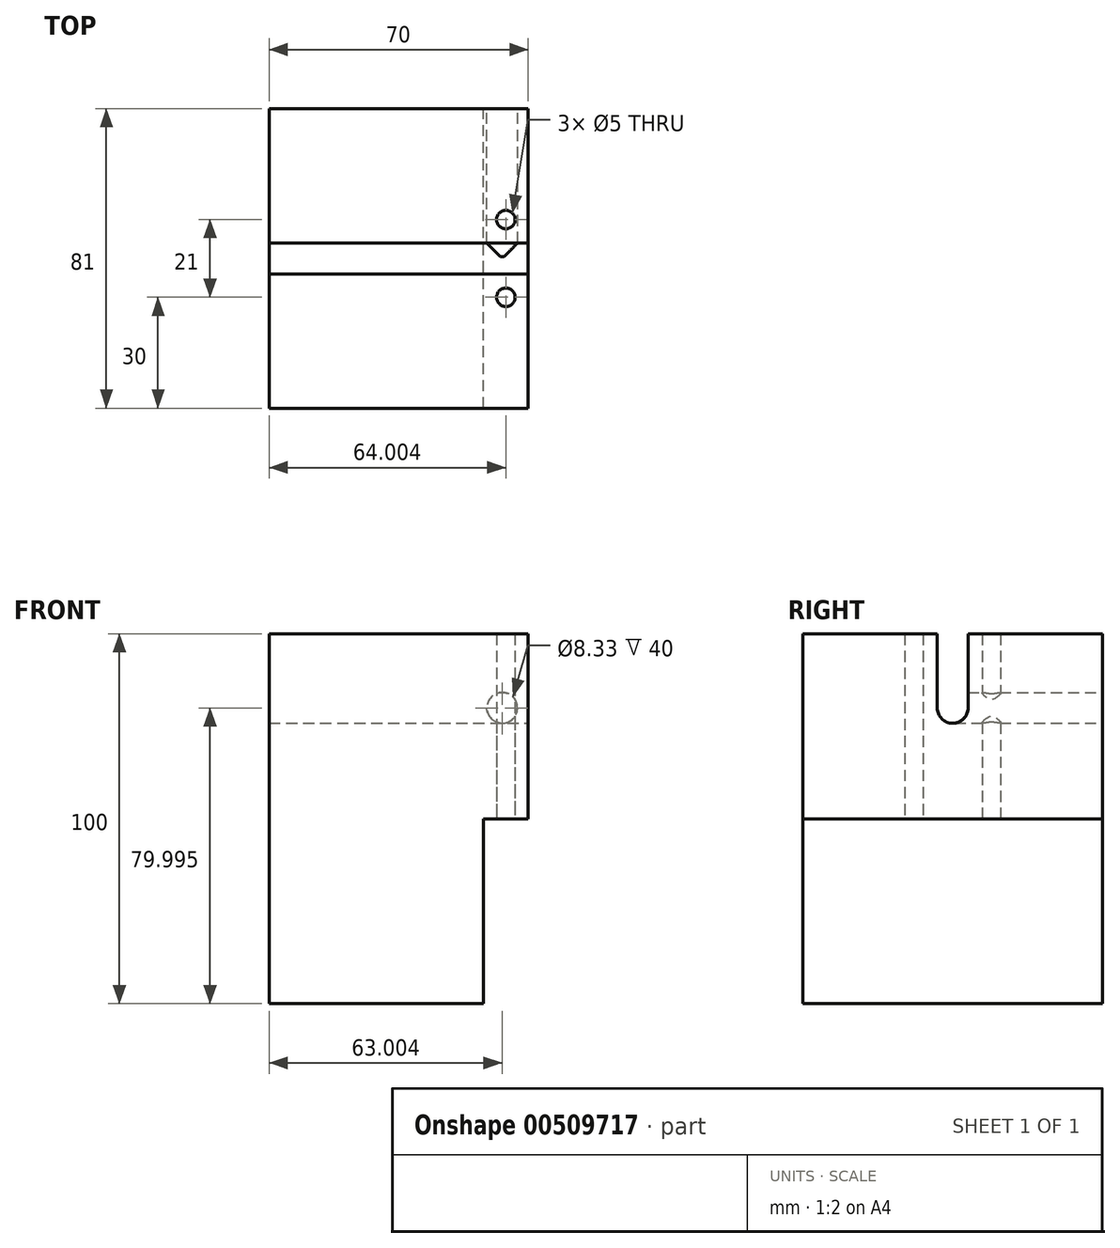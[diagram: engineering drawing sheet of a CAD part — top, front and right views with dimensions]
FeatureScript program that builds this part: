
annotation { "Feature Type Name" : "Feature", "Feature Type Description" : "" }
export const myFeature = defineFeature(function(context is Context, id is Id, definition is map)
    precondition{}
    {
        {
            var Q0;
            Q0=qCreatedBy(makeId("Front.planeOp"),FACE);
            var sketch = newSketch(context, id + "F0", { "sketchPlane" : qUnion([Q0])});
            skLineSegment(sketch, "E0", {"start": v(-82.66, 51.34) * mm, "end": v(-12.66, 51.34) * mm});
            skLineSegment(sketch, "E1", {"start": v(-12.66, 51.34) * mm, "end": v(-12.66, 1.34) * mm});
            skLineSegment(sketch, "E2", {"start": v(-12.66, 1.34) * mm, "end": v(-24.66, 1.34) * mm});
            skLineSegment(sketch, "E3", {"start": v(-24.66, 1.34) * mm, "end": v(-24.66, -48.66) * mm});
            skLineSegment(sketch, "E4", {"start": v(-24.66, -48.66) * mm, "end": v(-82.66, -48.66) * mm});
            skLineSegment(sketch, "E5", {"start": v(-82.66, -48.66) * mm, "end": v(-82.66, 51.34) * mm});
            skSolve(sketch);
        }
        {
            var Q0;
            Q0=makeQuery(id+"F0.imprint","IMPRINT",FACE,{"disambiguationData":[TD([[makeQuery(id+"F0.imprint","IMPRINT",EDGE,{"derivedFrom":sQuery(id+"F0.wireOp",EDGE,"E0")}),-1.0]])]});
            extrude(context, id + "F1", {"entities" : qUnion([Q0]), "depth" : 81 * mm});
        }
        {
            var Q0;
            Q0=qCreatedBy(makeId("Top.planeOp"),FACE);
            var sketch = newSketch(context, id + "F2", { "sketchPlane" : qUnion([Q0])});
            skCircle(sketch, "E6", {"center": v(-18.66, -30) * mm, "radius": 2.5 * mm});
            skCircle(sketch, "E7", {"center": v(-18.66, -51) * mm, "radius": 2.5 * mm});
            skSolve(sketch);
        }
        {
            var Q0;
            Q0 = qSketchRegion(id + "F2", true);
            extrude(context, id + "F3", {"entities" : qUnion([Q0]), "operationType" : NewBodyOperationType.REMOVE, "endBound" : BoundingType.THROUGH_ALL, "depth" : 25 * mm});
        }
        {
            var Q0;
            Q0=qCreatedBy(makeId("Right.planeOp"),FACE);
            var sketch = newSketch(context, id + "F4", { "sketchPlane" : qUnion([Q0])});
            skArc(sketch, "E8", {"start": v(-36.34, 51.34) * mm, "mid": v(-40.5, 55.5) * mm, "end": v(-44.67, 51.34) * mm});
            skArc(sketch, "E9", {"start": v(-44.67, 31.34) * mm, "mid": v(-40.5, 27.17) * mm, "end": v(-36.34, 31.34) * mm});
            skLineSegment(sketch, "E10.left", {"start": v(-36.33, 31.34) * mm, "end": v(-36.33, 51.34) * mm});
            skLineSegment(sketch, "E10.right", {"start": v(-44.66, 31.34) * mm, "end": v(-44.66, 51.34) * mm});
            skPoint(sketch, "E10.middle", {"position": v(-40.5, 41.34) * mm});
            skSolve(sketch);
        }
        {
            var Q0;
            Q0 = qSketchRegion(id + "F4", true);
            extrude(context, id + "F5", {"entities" : qUnion([Q0]), "operationType" : NewBodyOperationType.REMOVE, "oppositeDirection" : true, "depth" : 100 * mm});
        }
        {
            var Q0;
            Q0=qCreatedBy(makeId("Front.planeOp"),FACE);
            var sketch = newSketch(context, id + "F6", { "sketchPlane" : qUnion([Q0])});
            skCircle(sketch, "E11", {"center": v(-19.66, 31.34) * mm, "radius": 4.17 * mm});
            skSolve(sketch);
        }
        {
            var Q0;
            Q0 = qSketchRegion(id + "F6", true);
            extrude(context, id + "F7", {"entities" : qUnion([Q0]), "operationType" : NewBodyOperationType.REMOVE, "depth" : 40 * mm});
        }
    });
